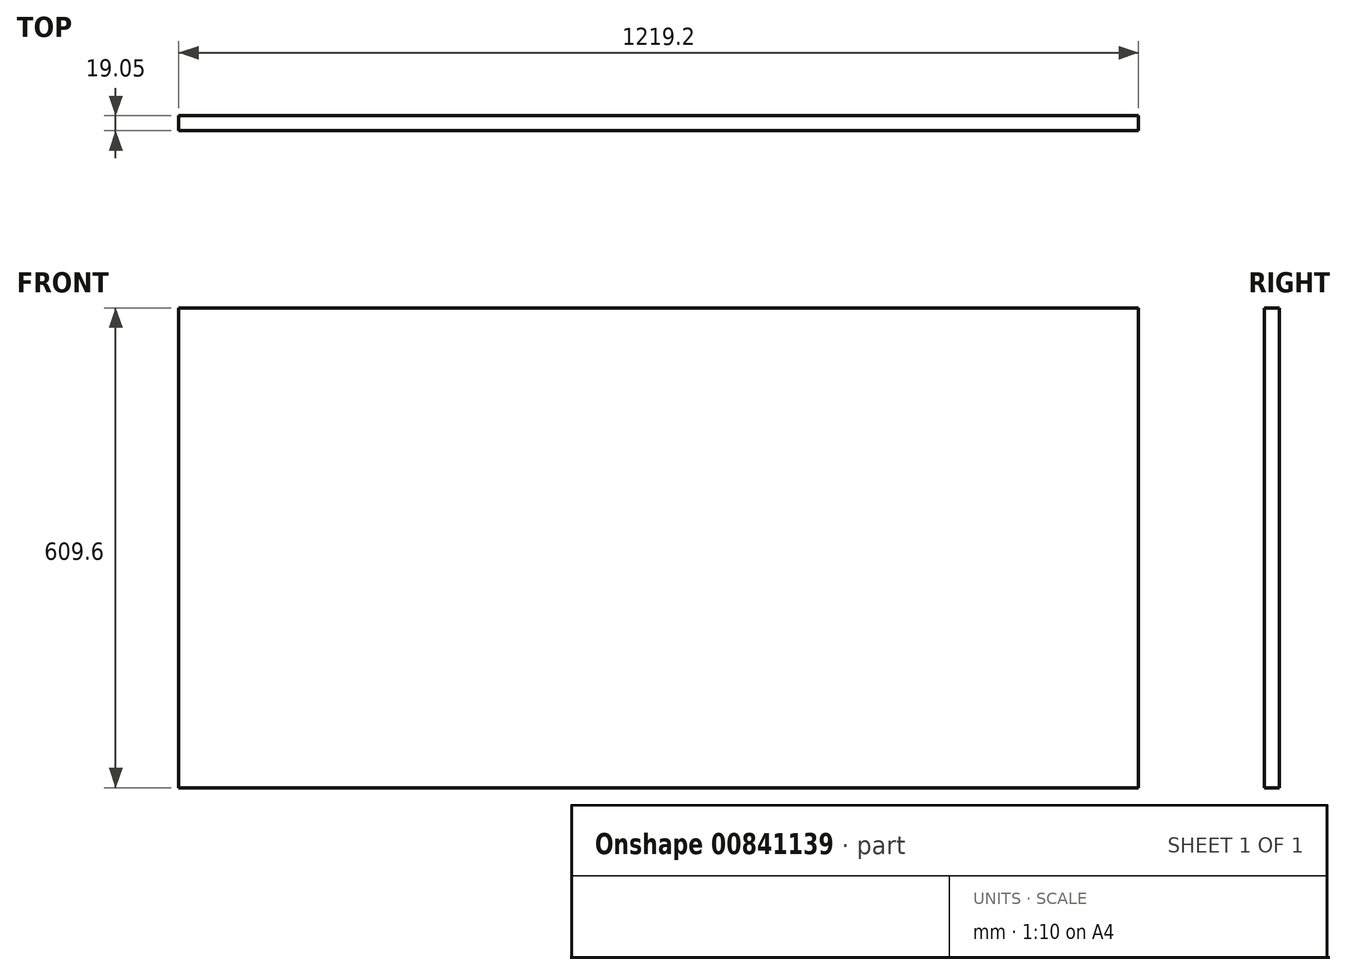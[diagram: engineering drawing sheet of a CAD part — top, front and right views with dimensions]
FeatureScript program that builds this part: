
annotation { "Feature Type Name" : "Feature", "Feature Type Description" : "" }
export const myFeature = defineFeature(function(context is Context, id is Id, definition is map)
    precondition{}
    {
        {
            var Q0;
            Q0=qCreatedBy(makeId("Front.planeOp"),FACE);
            var sketch = newSketch(context, id + "F0", { "sketchPlane" : qUnion([Q0])});
            skLineSegment(sketch, "E0.bottom", {"start": v(0, 0) * mm, "end": v(-1219.2, 0) * mm});
            skLineSegment(sketch, "E0.top", {"start": v(0, 609.6) * mm, "end": v(-1219.2, 609.6) * mm});
            skLineSegment(sketch, "E0.left", {"start": v(0, 0) * mm, "end": v(0, 609.6) * mm});
            skLineSegment(sketch, "E0.right", {"start": v(-1219.2, 0) * mm, "end": v(-1219.2, 609.6) * mm});
            skSolve(sketch);
        }
        {
            var Q0;
            Q0=makeQuery(id+"F0.imprint","IMPRINT",FACE,{"disambiguationData":[TD([[makeQuery(id+"F0.imprint","IMPRINT",EDGE,{"derivedFrom":sQuery(id+"F0.wireOp",EDGE,"E0.bottom")}),-1.0]])]});
            extrude(context, id + "F1", {"entities" : qUnion([Q0]), "depth" : 19.05 * mm, "offsetDistance" : 25.4 * mm});
        }
    });
